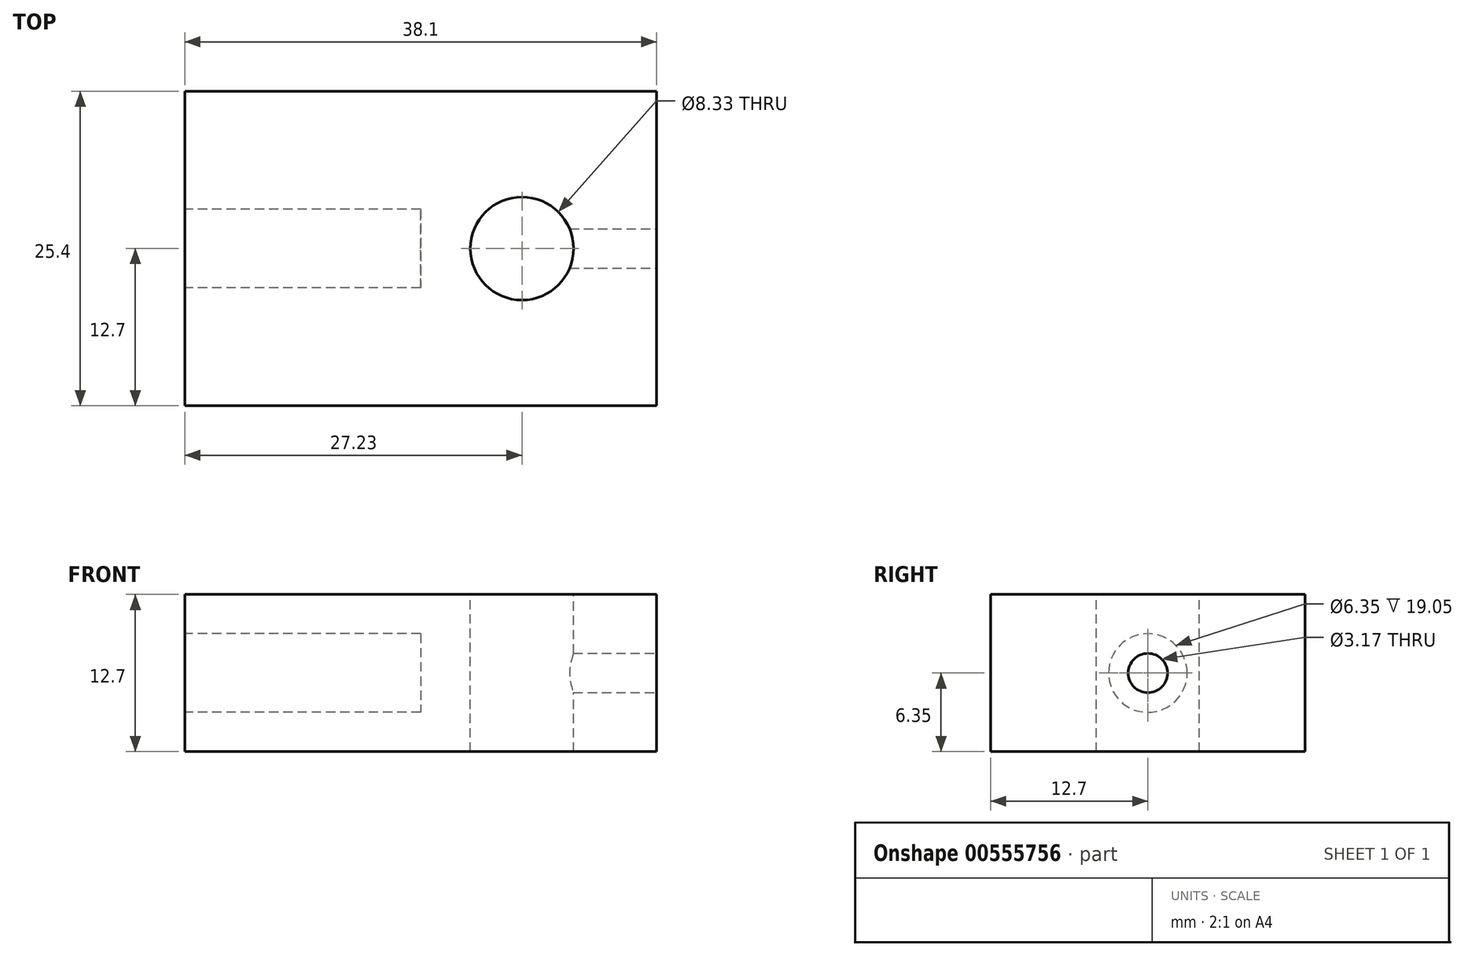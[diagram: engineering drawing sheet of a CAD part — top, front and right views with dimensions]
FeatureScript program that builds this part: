
annotation { "Feature Type Name" : "Feature", "Feature Type Description" : "" }
export const myFeature = defineFeature(function(context is Context, id is Id, definition is map)
    precondition{}
    {
        {
            var Q0;
            Q0=qCreatedBy(makeId("Top.planeOp"),FACE);
            var sketch = newSketch(context, id + "F0", { "sketchPlane" : qUnion([Q0])});
            skLineSegment(sketch, "E0.bottom", {"start": v(10.87, -12.7) * mm, "end": v(-27.23, -12.7) * mm});
            skLineSegment(sketch, "E0.top", {"start": v(10.87, 12.7) * mm, "end": v(-27.23, 12.7) * mm});
            skLineSegment(sketch, "E0.left", {"start": v(10.87, -12.7) * mm, "end": v(10.87, 12.7) * mm});
            skLineSegment(sketch, "E0.right", {"start": v(-27.23, -12.7) * mm, "end": v(-27.23, 12.7) * mm});
            skPoint(sketch, "E0.middle", {"position": v(0, 0) * mm});
            skCircle(sketch, "E1", {"center": v(0, 0) * mm, "radius": 4.17 * mm});
            skSolve(sketch);
        }
        {
            var Q0;
            Q0=makeQuery(id+"F0.imprint","IMPRINT",FACE,{"disambiguationData":[TD([[makeQuery(id+"F0.imprint","IMPRINT",EDGE,{"derivedFrom":sQuery(id+"F0.wireOp",EDGE,"E0.bottom")}),-1.0]])]});
            extrude(context, id + "F1", {"entities" : qUnion([Q0]), "oppositeDirection" : true, "depth" : 12.7 * mm, "offsetDistance" : 25.4 * mm});
        }
        {
            var Q0;
            Q0=makeQuery(id+"F1.opExtrude","SWEPT_FACE",FACE,{"disambiguationData":[OSD([sQuery(id+"F0.wireOp",EDGE,"E0.right")])]});
            var sketch = newSketch(context, id + "F2", { "sketchPlane" : qUnion([Q0])});
            skCircle(sketch, "E2", {"center": v(0, -6.35) * mm, "radius": 3.18 * mm});
            skSolve(sketch);
        }
        {
            var Q0;
            Q0=makeQuery(id+"F2.imprint","IMPRINT",FACE,{"disambiguationData":[TD([[makeQuery(id+"F2.imprint","IMPRINT",EDGE,{"derivedFrom":sQuery(id+"F2.wireOp",EDGE,"E2")}),1.0]])]});
            extrude(context, id + "F3", {"entities" : qUnion([Q0]), "operationType" : NewBodyOperationType.REMOVE, "oppositeDirection" : true, "depth" : 19.05 * mm, "offsetDistance" : 25.4 * mm});
        }
        {
            var Q0;
            Q0=makeQuery(id+"F1.opExtrude","SWEPT_FACE",FACE,{"disambiguationData":[OSD([sQuery(id+"F0.wireOp",EDGE,"E0.left")])]});
            var sketch = newSketch(context, id + "F4", { "sketchPlane" : qUnion([Q0])});
            skCircle(sketch, "E3", {"center": v(0, -6.35) * mm, "radius": 1.59 * mm});
            skSolve(sketch);
        }
        {
            var Q0;
            Q0=makeQuery(id+"F4.imprint","IMPRINT",FACE,{"disambiguationData":[TD([[makeQuery(id+"F4.imprint","IMPRINT",EDGE,{"derivedFrom":sQuery(id+"F4.wireOp",EDGE,"E3")}),1.0]])]});
            extrude(context, id + "F5", {"entities" : qUnion([Q0]), "operationType" : NewBodyOperationType.REMOVE, "oppositeDirection" : true, "depth" : 12.7 * mm, "offsetDistance" : 25.4 * mm});
        }
    });
